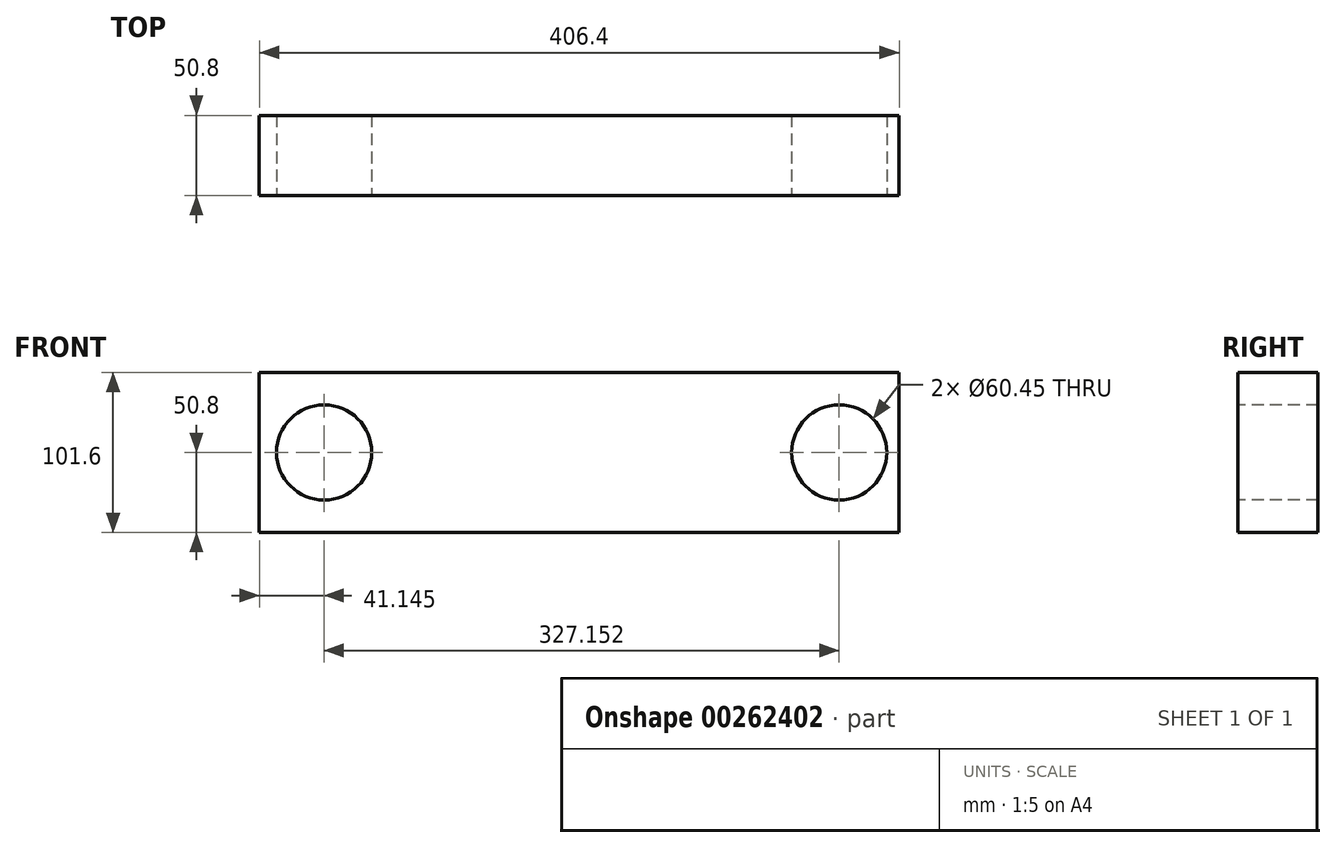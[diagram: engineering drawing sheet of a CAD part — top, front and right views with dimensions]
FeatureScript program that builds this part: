
annotation { "Feature Type Name" : "Feature", "Feature Type Description" : "" }
export const myFeature = defineFeature(function(context is Context, id is Id, definition is map)
    precondition{}
    {
        {
            var Q0;
            Q0=qCreatedBy(makeId("Front.planeOp"),FACE);
            var sketch = newSketch(context, id + "F0", { "sketchPlane" : qUnion([Q0])});
            skLineSegment(sketch, "E0.bottom", {"start": v(-63.36, 62.98) * mm, "end": v(343.04, 62.98) * mm});
            skLineSegment(sketch, "E0.top", {"start": v(-63.36, -38.62) * mm, "end": v(343.04, -38.62) * mm});
            skLineSegment(sketch, "E0.left", {"start": v(-63.36, 62.98) * mm, "end": v(-63.36, -38.62) * mm});
            skLineSegment(sketch, "E0.right", {"start": v(343.04, 62.98) * mm, "end": v(343.04, -38.62) * mm});
            skSolve(sketch);
        }
        {
            var Q0;
            Q0=makeQuery(id+"F0.imprint","IMPRINT",FACE,{"disambiguationData":[TD([[makeQuery(id+"F0.imprint","IMPRINT",EDGE,{"derivedFrom":sQuery(id+"F0.wireOp",EDGE,"E0.bottom")}),-1.0]])]});
            extrude(context, id + "F1", {"entities" : qUnion([Q0]), "depth" : 50.8 * mm});
        }
        {
            var Q0;
            Q0=makeQuery(id+"F1.opExtrude","CAP_FACE",FACE,{"disambiguationData":[OSD([sQuery(id+"F0.wireOp",EDGE,"E0.bottom"),sQuery(id+"F0.wireOp",EDGE,"E0.top"),sQuery(id+"F0.wireOp",EDGE,"E0.left"),sQuery(id+"F0.wireOp",EDGE,"E0.right")])],"isStart":false});
            var sketch = newSketch(context, id + "F2", { "sketchPlane" : qUnion([Q0])});
            skPoint(sketch, "E1.endSnap0", {"position": v(343.04, 12.18) * mm});
            skCircle(sketch, "E2", {"center": v(-22.21, 12.18) * mm, "radius": 30.23 * mm});
            skCircle(sketch, "E3", {"center": v(304.94, 12.18) * mm, "radius": 30.23 * mm});
            skLineSegment(sketch, "E4", {"start": v(-63.36, 12.18) * mm, "end": v(-52.44, 12.18) * mm});
            skLineSegment(sketch, "E5", {"start": v(343.04, 12.18) * mm, "end": v(335.16, 12.18) * mm});
            skLineSegment(sketch, "E6", {"start": v(-22.21, 12.18) * mm, "end": v(8.01, 12.18) * mm});
            skLineSegment(sketch, "E7", {"start": v(8.01, 12.18) * mm, "end": v(274.71, 12.18) * mm});
            skLineSegment(sketch, "E8", {"start": v(274.71, 12.18) * mm, "end": v(304.94, 12.18) * mm});
            skSolve(sketch);
        }
        {
            var Q0;
            Q0=makeQuery(id+"F2.imprint","IMPRINT",FACE,{"disambiguationData":[TD([[makeQuery(id+"F2.imprint","IMPRINT",EDGE,{"derivedFrom":sQuery(id+"F2.wireOp",EDGE,"E2")}),1.0]])]});
            var Q1;
            Q1=makeQuery(id+"F2.imprint","IMPRINT",FACE,{"disambiguationData":[TD([[makeQuery(id+"F2.imprint","IMPRINT",EDGE,{"derivedFrom":sQuery(id+"F2.wireOp",EDGE,"E3")}),1.0]])]});
            extrude(context, id + "F3", {"entities" : qUnion([Q0, Q1]), "operationType" : NewBodyOperationType.REMOVE, "endBound" : BoundingType.THROUGH_ALL, "oppositeDirection" : true, "depth" : 50.8 * mm});
        }
    });
